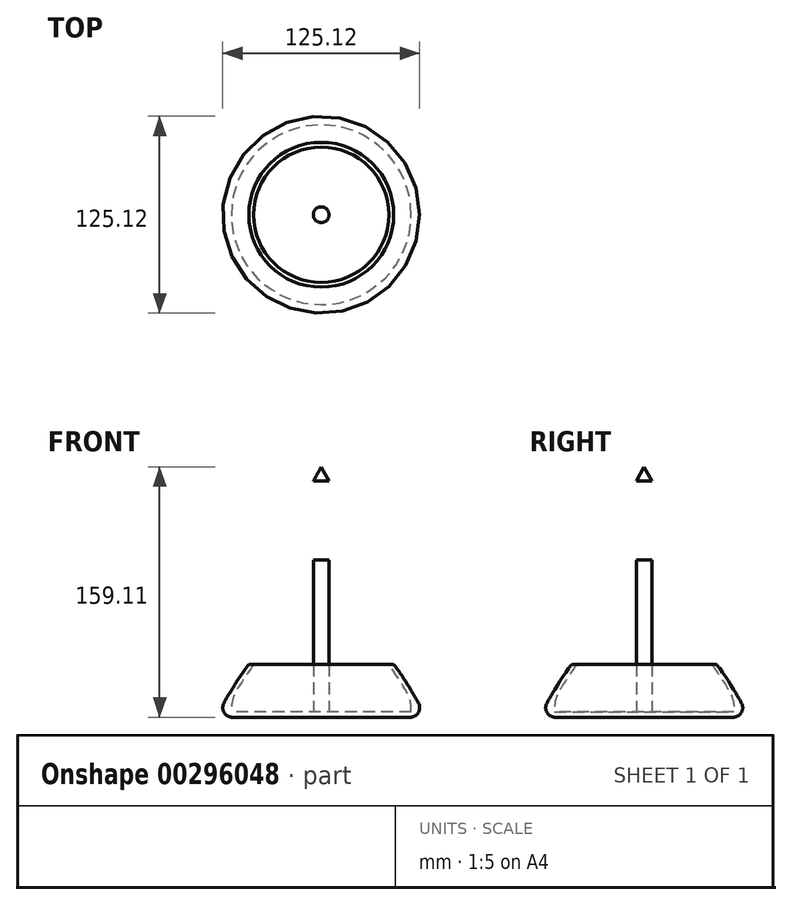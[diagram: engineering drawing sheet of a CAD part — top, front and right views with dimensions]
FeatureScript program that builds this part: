
annotation { "Feature Type Name" : "Feature", "Feature Type Description" : "" }
export const myFeature = defineFeature(function(context is Context, id is Id, definition is map)
    precondition{}
    {
        {
            var Q0;
            Q0=qCreatedBy(makeId("Front.planeOp"),FACE);
            var sketch = newSketch(context, id + "F0", { "sketchPlane" : qUnion([Q0]), "disableImprinting" : false});
            skLineSegment(sketch, "E0", {"start": v(0, 0) * mm, "end": v(65, 0) * mm});
            skLineSegment(sketch, "E1", {"start": v(57.08, 3.5) * mm, "end": v(0, 3.5) * mm});
            skLineSegment(sketch, "E2", {"start": v(0, 3.5) * mm, "end": v(0, 0) * mm});
            skPoint(sketch, "E3.end.orphan", {"position": v(35, 0) * mm});
            skFitSpline(sketch, "E4", {"points": [v(65, 0) * mm, v(60.05, 12.08) * mm, v(45.98, 33.5) * mm], "startDerivative": vector(-2.16, 25.64) * mm, "endDerivative": vector(-24, 29.1) * mm});
            skFitSpline(sketch, "E5", {"points": [v(57.08, 3.5) * mm, v(56.05, 12) * mm, v(42.98, 33.5) * mm], "startDerivative": vector(-2.26, 19.76) * mm, "endDerivative": vector(-19.8, 29.02) * mm});
            skLineSegment(sketch, "E6", {"start": v(45.98, 33.5) * mm, "end": v(42.98, 33.5) * mm});
            skPoint(sketch, "E7", {"position": v(57.1, 17.12) * mm});
            skSolve(sketch);
        }
        {
            var Q0;
            Q0=makeQuery(id+"F0.imprint","IMPRINT",FACE,{"disambiguationData":[TD([[makeQuery(id+"F0.imprint","IMPRINT",EDGE,{"derivedFrom":sQuery(id+"F0.wireOp",EDGE,"E0")}),1.0]])]});
            var Q1;
            Q1=sQuery(id+"F0.wireOp",EDGE,"E2");
            revolve(context, id + "F1", {"entities" : qUnion([Q0]), "axis" : qUnion([Q1]), "revolveType" : RevolveType.FULL});
        }
        {
            var Q0;
            Q0=makeQuery(id+"F1.opRevolve","SWEPT_EDGE",EDGE,{"disambiguationData":[OSD([sQuery(id+"F0.wireOp",EDGE,"E0"),sQuery(id+"F0.wireOp",EDGE,"3e9fe49b-ee8e-478b-ad08-dfce90acd2dd")])]});
            fillet(context, id + "F2", {"entities" : qUnion([Q0]), "radius" : 6 * mm, "tangentPropagation" : true, "allowEdgeOverflow" : false});
        }
        {
            var Q0;
            Q0=qCreatedBy(makeId("Top.planeOp"),FACE);
            var sketch = newSketch(context, id + "F3", { "sketchPlane" : qUnion([Q0])});
            skCircle(sketch, "E8", {"center": v(0, 0) * mm, "radius": 5 * mm});
            skSolve(sketch);
        }
        {
            var Q0;
            Q0=makeQuery(id+"F3.imprint","IMPRINT",FACE,{"disambiguationData":[TD([[makeQuery(id+"F3.imprint","IMPRINT",EDGE,{"derivedFrom":sQuery(id+"F3.wireOp",EDGE,"E8")}),1.0]])]});
            extrude(context, id + "F4", {"entities" : qUnion([Q0]), "depth" : 100 * mm});
        }
        {
            var Q0;
            Q0=qCreatedBy(makeId("Front.planeOp"),FACE);
            var sketch = newSketch(context, id + "F5", { "sketchPlane" : qUnion([Q0])});
            skLineSegment(sketch, "E9", {"start": v(0, 150.04) * mm, "end": v(0, 159.11) * mm});
            skLineSegment(sketch, "E10", {"start": v(0, 159.11) * mm, "end": v(5, 150) * mm});
            skLineSegment(sketch, "E11", {"start": v(5, 150) * mm, "end": v(0, 150.04) * mm});
            skPoint(sketch, "E12", {"position": v(5, 150) * mm});
            skSolve(sketch);
        }
        {
            var Q0;
            Q0=makeQuery(id+"F5.imprint","IMPRINT",FACE,{"disambiguationData":[TD([[makeQuery(id+"F5.imprint","IMPRINT",EDGE,{"derivedFrom":sQuery(id+"F5.wireOp",EDGE,"E9")}),-1.0]])]});
            var Q1;
            Q1=sQuery(id+"F5.wireOp",EDGE,"E9");
            revolve(context, id + "F6", {"operationType" : NewBodyOperationType.ADD, "entities" : qUnion([Q0]), "axis" : qUnion([Q1]), "revolveType" : RevolveType.FULL});
        }
    });
